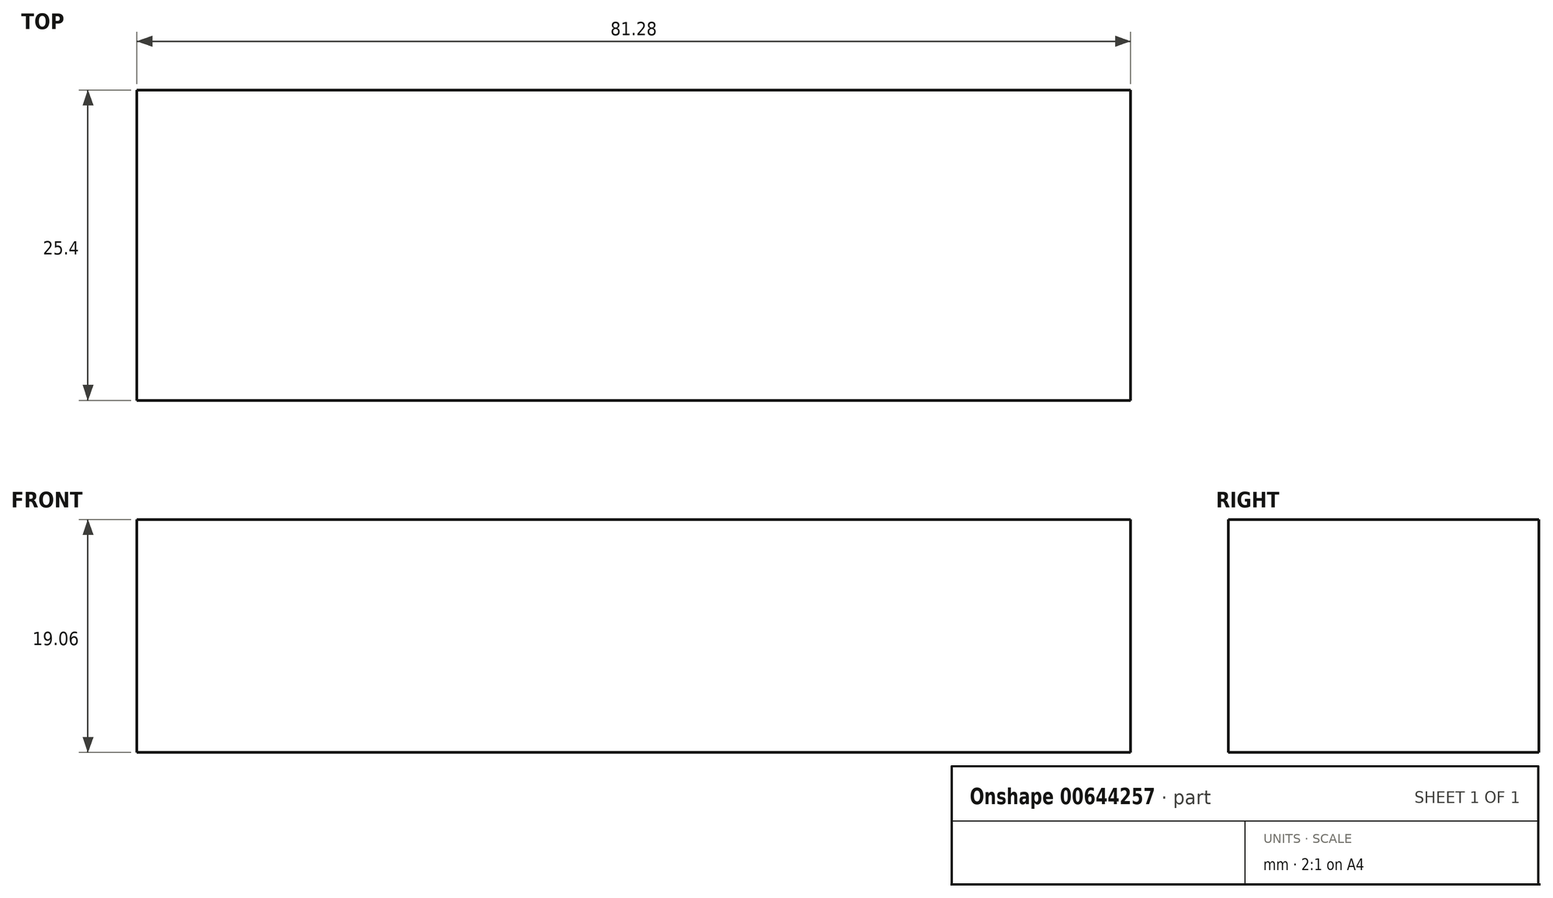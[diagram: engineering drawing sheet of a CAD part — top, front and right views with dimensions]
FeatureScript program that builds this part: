
annotation { "Feature Type Name" : "Feature", "Feature Type Description" : "" }
export const myFeature = defineFeature(function(context is Context, id is Id, definition is map)
    precondition{}
    {
        {
            var Q0;
            Q0=qCreatedBy(makeId("Front.planeOp"),FACE);
            var sketch = newSketch(context, id + "F0", { "sketchPlane" : qUnion([Q0])});
            skLineSegment(sketch, "E0.bottom", {"start": v(-40.64, -9.53) * mm, "end": v(40.64, -9.53) * mm});
            skLineSegment(sketch, "E0.top", {"start": v(-40.64, 9.53) * mm, "end": v(40.64, 9.53) * mm});
            skLineSegment(sketch, "E0.left", {"start": v(-40.64, -9.53) * mm, "end": v(-40.64, 9.53) * mm});
            skLineSegment(sketch, "E0.right", {"start": v(40.64, -9.53) * mm, "end": v(40.64, 9.52) * mm});
            skPoint(sketch, "E0.middle", {"position": v(0, 0) * mm});
            skLineSegment(sketch, "E1.bottom", {"start": v(39.3, 29.45) * mm, "end": v(97.4, 29.45) * mm});
            skLineSegment(sketch, "E1.top", {"start": v(39.3, 52.9) * mm, "end": v(97.4, 52.9) * mm});
            skLineSegment(sketch, "E1.left", {"start": v(39.3, 29.45) * mm, "end": v(39.3, 52.9) * mm});
            skLineSegment(sketch, "E1.right", {"start": v(97.4, 29.45) * mm, "end": v(97.4, 52.9) * mm});
            skPoint(sketch, "E1.middle", {"position": v(68.36, 41.17) * mm});
            skLineSegment(sketch, "E2", {"start": v(40.64, 9.53) * mm, "end": v(40.64, 26.18) * mm});
            skArc(sketch, "E3", {"start": v(40.64, 26.18) * mm, "mid": v(43.14, 31.24) * mm, "end": v(48.68, 32.3) * mm});
            skLineSegment(sketch, "E4", {"start": v(48.68, 32.3) * mm, "end": v(74.4, 32.3) * mm});
            skSolve(sketch);
        }
        {
            var Q0;
            Q0=makeQuery(id+"F0.imprint","IMPRINT",FACE,{"disambiguationData":[TD([[makeQuery(id+"F0.imprint","IMPRINT",EDGE,{"derivedFrom":sQuery(id+"F0.wireOp",EDGE,"E0.bottom")}),1.0]])]});
            extrude(context, id + "F1", {"entities" : qUnion([Q0]), "depth" : 25.4 * mm, "offsetDistance" : 25.4 * mm});
        }
    });
